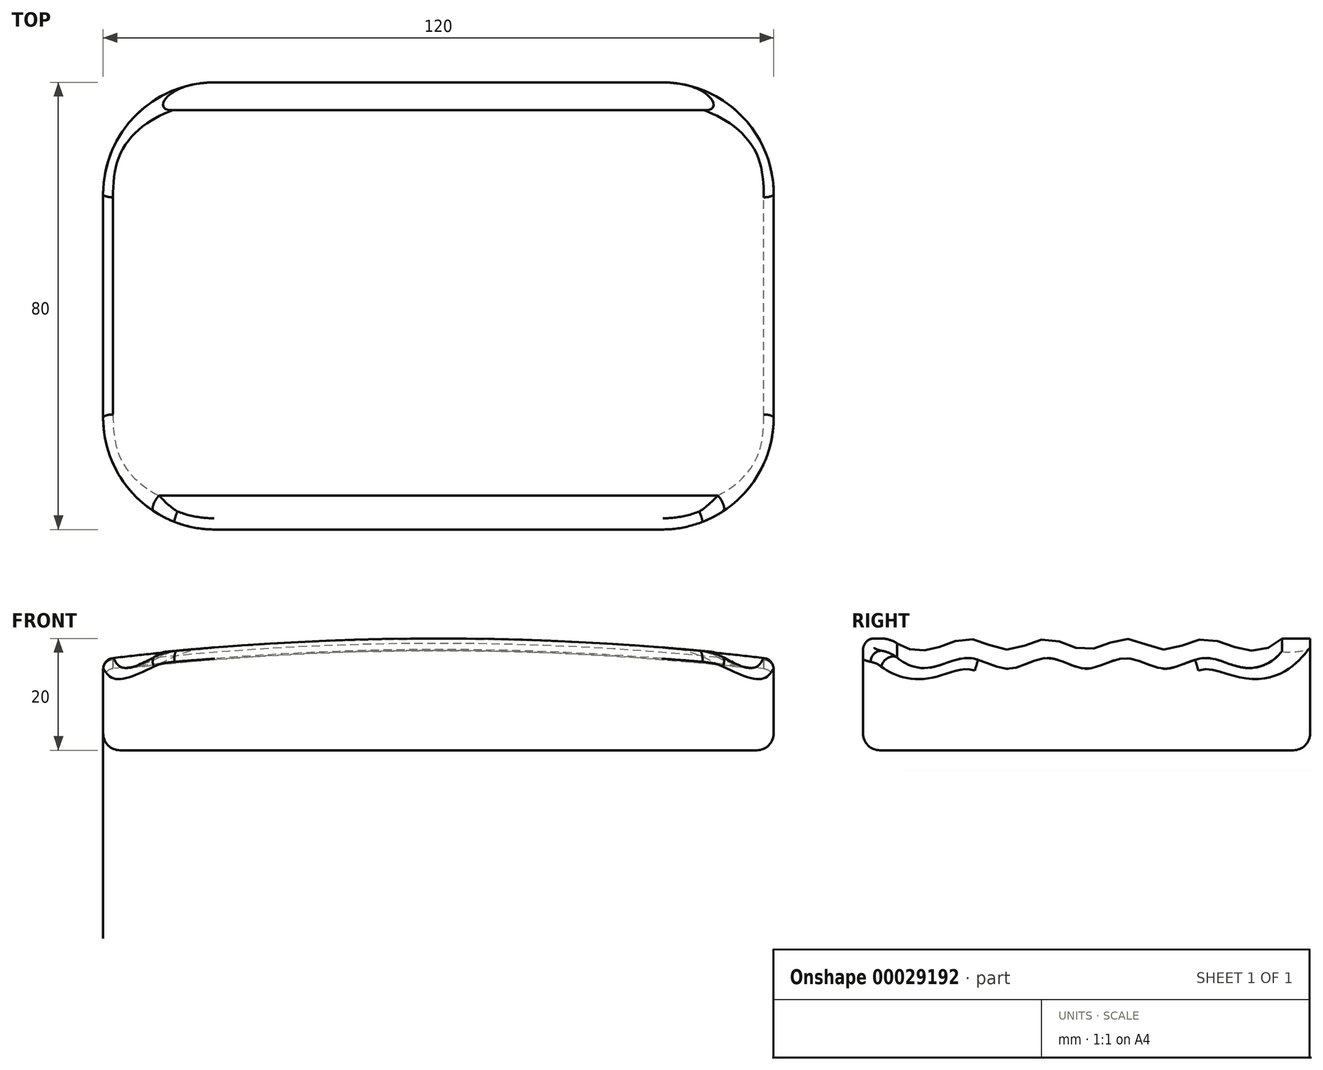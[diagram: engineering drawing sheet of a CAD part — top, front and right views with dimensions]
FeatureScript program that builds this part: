
annotation { "Feature Type Name" : "Feature", "Feature Type Description" : "" }
export const myFeature = defineFeature(function(context is Context, id is Id, definition is map)
    precondition{}
    {
        {
            var Q0;
            Q0=qCreatedBy(makeId("Top.planeOp"),FACE);
            var sketch = newSketch(context, id + "F0", { "sketchPlane" : qUnion([Q0])});
            skLineSegment(sketch, "E0.bottom", {"start": v(0, 0) * mm, "end": v(120, 0) * mm});
            skLineSegment(sketch, "E0.top", {"start": v(0, 80) * mm, "end": v(120, 80) * mm});
            skLineSegment(sketch, "E0.left", {"start": v(0, 0) * mm, "end": v(0, 80) * mm});
            skLineSegment(sketch, "E0.right", {"start": v(120, 0) * mm, "end": v(120, 80) * mm});
            skSolve(sketch);
        }
        {
            var Q0;
            Q0 = qSketchRegion(id + "F0", true);
            extrude(context, id + "F1", {"entities" : qUnion([Q0]), "depth" : 20 * mm});
        }
        {
            var Q0;
            Q0=makeQuery(id+"F1.opExtrude","SWEPT_FACE",FACE,{"disambiguationData":[OSD([sQuery(id+"F0.wireOp",EDGE,"E0.bottom")])]});
            var sketch = newSketch(context, id + "F2", { "sketchPlane" : qUnion([Q0])});
            skArc(sketch, "E1", {"start": v(120, 16.39) * mm, "mid": v(60, 20) * mm, "end": v(0, 16.39) * mm});
            skLineSegment(sketch, "E2", {"start": v(0, 16.39) * mm, "end": v(0, 47.47) * mm});
            skLineSegment(sketch, "E3", {"start": v(0, 47.47) * mm, "end": v(120, 47.47) * mm});
            skLineSegment(sketch, "E4", {"start": v(120, 47.47) * mm, "end": v(120, 16.39) * mm});
            skSolve(sketch);
        }
        {
            var Q0;
            Q0 = qSketchRegion(id + "F2", true);
            var Q1;
            Q1=makeQuery(id+"F1.opExtrude","SWEPT_FACE",FACE,{"disambiguationData":[OSD([sQuery(id+"F0.wireOp",EDGE,"E0.top")])]});
            extrude(context, id + "F3", {"entities" : qUnion([Q0]), "operationType" : NewBodyOperationType.REMOVE, "endBound" : BoundingType.UP_TO_SURFACE, "oppositeDirection" : true, "endBoundEntityFace" : qUnion([Q1]), "depth" : 25 * mm});
        }
        {
            var Q0;
            Q0=makeQuery(id+"F1.opExtrude","SWEPT_FACE",FACE,{"disambiguationData":[OSD([sQuery(id+"F0.wireOp",EDGE,"E0.left")])]});
            var sketch = newSketch(context, id + "F4", { "sketchPlane" : qUnion([Q0])});
            skLineSegment(sketch, "E5", {"start": v(-80, 16.39) * mm, "end": v(-80, 41.7) * mm});
            skLineSegment(sketch, "E6", {"start": v(-80, 41.7) * mm, "end": v(0, 41.7) * mm});
            skLineSegment(sketch, "E7", {"start": v(0, 41.7) * mm, "end": v(0, 16.39) * mm});
            skFitSpline(sketch, "E8", {"points": [v(-75, 16.39) * mm, v(-68, 14.39) * mm, v(-61, 16.29) * mm, v(-54, 14.39) * mm, v(-47, 16.29) * mm, v(-40, 14.39) * mm, v(-33, 16.29) * mm, v(-26, 14.39) * mm, v(-19, 16.29) * mm, v(-12, 14.39) * mm, v(-5, 16.39) * mm], "startDerivative": vector(59.91, -59.91) * mm, "endDerivative": vector(59.91, 59.91) * mm});
            skLineSegment(sketch, "E9", {"start": v(-75, 16.39) * mm, "end": v(-80, 16.39) * mm});
            skLineSegment(sketch, "E10", {"start": v(-5, 16.39) * mm, "end": v(0, 16.39) * mm});
            skSolve(sketch);
        }
        {
            var Q0;
            Q0=makeQuery(id+"F1.opExtrude","SWEPT_FACE",FACE,{"disambiguationData":[OSD([sQuery(id+"F0.wireOp",EDGE,"E0.bottom")])]});
            var sketch = newSketch(context, id + "F5", { "sketchPlane" : qUnion([Q0])});
            skCircle(sketch, "E11", {"center": v(60, -480) * mm, "radius": 500 * mm});
            skSolve(sketch);
        }
        {
            var Q0;
            {var subQ0=makeQuery(id+"F3.boolean.opBoolean","COPY",EDGE,{"derivedFrom":makeQuery(id+"F3.opExtrude","SWEPT_EDGE",EDGE,{"disambiguationData":[OSD([sQuery(id+"F0.wireOp",EDGE,"E0.bottom"),sQuery(id+"F0.wireOp",EDGE,"E0.left"),sQuery(id+"F2.wireOp",EDGE,"E1"),sQuery(id+"F2.wireOp",EDGE,"E2")])]})});var subQ1=sQuery(id+"F4.wireOp",EDGE,"E8");var subQ2=makeQuery(id+"F4.imprint","INTERSECT",VERTEX,{"disambiguationData":[OD(0.0)],"derivedFrom":[subQ0,subQ1]});Q0=makeQuery(id+"F4.imprint","IMPRINT",FACE,{"disambiguationData":[TD([[makeQuery(id+"F4.imprint","IMPRINT",EDGE,{"disambiguationData":[TD([[subQ2,1.0]])],"derivedFrom":subQ1}),1.0]])]});}
            var Q1;
            {var subQ0=makeQuery(id+"F3.boolean.opBoolean","COPY",EDGE,{"derivedFrom":makeQuery(id+"F3.opExtrude","SWEPT_EDGE",EDGE,{"disambiguationData":[OSD([sQuery(id+"F0.wireOp",EDGE,"E0.bottom"),sQuery(id+"F0.wireOp",EDGE,"E0.left"),sQuery(id+"F2.wireOp",EDGE,"E1"),sQuery(id+"F2.wireOp",EDGE,"E2")])]})});var subQ1=sQuery(id+"F4.wireOp",EDGE,"E8");var subQ3=makeQuery(id+"F4.imprint","INTERSECT",VERTEX,{"disambiguationData":[OD(1.0)],"derivedFrom":[subQ0,subQ1]});Q1=makeQuery(id+"F4.imprint","IMPRINT",FACE,{"disambiguationData":[TD([[makeQuery(id+"F4.imprint","IMPRINT",EDGE,{"disambiguationData":[TD([[subQ3,-1.0]])],"derivedFrom":subQ1}),1.0]])]});}
            var Q2;
            {var subQ0=makeQuery(id+"F3.boolean.opBoolean","COPY",EDGE,{"derivedFrom":makeQuery(id+"F3.opExtrude","SWEPT_EDGE",EDGE,{"disambiguationData":[OSD([sQuery(id+"F0.wireOp",EDGE,"E0.bottom"),sQuery(id+"F0.wireOp",EDGE,"E0.left"),sQuery(id+"F2.wireOp",EDGE,"E1"),sQuery(id+"F2.wireOp",EDGE,"E2")])]})});var subQ1=sQuery(id+"F4.wireOp",EDGE,"E8");var subQ3=makeQuery(id+"F4.imprint","INTERSECT",VERTEX,{"disambiguationData":[OD(3.0)],"derivedFrom":[subQ0,subQ1]});Q2=makeQuery(id+"F4.imprint","IMPRINT",FACE,{"disambiguationData":[TD([[makeQuery(id+"F4.imprint","IMPRINT",EDGE,{"disambiguationData":[TD([[subQ3,-1.0]])],"derivedFrom":subQ1}),1.0]])]});}
            var Q3;
            {var subQ0=makeQuery(id+"F3.boolean.opBoolean","COPY",EDGE,{"derivedFrom":makeQuery(id+"F3.opExtrude","SWEPT_EDGE",EDGE,{"disambiguationData":[OSD([sQuery(id+"F0.wireOp",EDGE,"E0.bottom"),sQuery(id+"F0.wireOp",EDGE,"E0.left"),sQuery(id+"F2.wireOp",EDGE,"E1"),sQuery(id+"F2.wireOp",EDGE,"E2")])]})});var subQ1=sQuery(id+"F4.wireOp",EDGE,"E8");var subQ3=makeQuery(id+"F4.imprint","INTERSECT",VERTEX,{"disambiguationData":[OD(5.0)],"derivedFrom":[subQ0,subQ1]});Q3=makeQuery(id+"F4.imprint","IMPRINT",FACE,{"disambiguationData":[TD([[makeQuery(id+"F4.imprint","IMPRINT",EDGE,{"disambiguationData":[TD([[subQ3,-1.0]])],"derivedFrom":subQ1}),1.0]])]});}
            var Q4;
            {var subQ0=makeQuery(id+"F3.boolean.opBoolean","COPY",EDGE,{"derivedFrom":makeQuery(id+"F3.opExtrude","SWEPT_EDGE",EDGE,{"disambiguationData":[OSD([sQuery(id+"F0.wireOp",EDGE,"E0.bottom"),sQuery(id+"F0.wireOp",EDGE,"E0.left"),sQuery(id+"F2.wireOp",EDGE,"E1"),sQuery(id+"F2.wireOp",EDGE,"E2")])]})});var subQ1=sQuery(id+"F4.wireOp",EDGE,"E8");var subQ2=makeQuery(id+"F4.imprint","INTERSECT",VERTEX,{"disambiguationData":[OD(7.0)],"derivedFrom":[subQ0,subQ1]});Q4=makeQuery(id+"F4.imprint","IMPRINT",FACE,{"disambiguationData":[TD([[makeQuery(id+"F4.imprint","IMPRINT",EDGE,{"disambiguationData":[TD([[subQ2,-1.0]])],"derivedFrom":subQ1}),1.0]])]});}
            var Q5;
            Q5=sQuery(id+"F5.wireOp",EDGE,"E11");
            sweep(context, id + "F6", {"operationType" : NewBodyOperationType.REMOVE, "profiles" : qUnion([Q0, Q1, Q2, Q3, Q4]), "path" : qUnion([Q5])});
        }
        {
            var Q0;
            Q0=makeQuery(id+"F1.opExtrude","SWEPT_EDGE",EDGE,{"disambiguationData":[OSD([sQuery(id+"F0.wireOp",EDGE,"E0.top"),sQuery(id+"F0.wireOp",EDGE,"E0.left")])]});
            var Q1;
            Q1=makeQuery(id+"F1.opExtrude","SWEPT_EDGE",EDGE,{"disambiguationData":[OSD([sQuery(id+"F0.wireOp",EDGE,"E0.bottom"),sQuery(id+"F0.wireOp",EDGE,"E0.left")])]});
            var Q2;
            Q2=makeQuery(id+"F1.opExtrude","SWEPT_EDGE",EDGE,{"disambiguationData":[OSD([sQuery(id+"F0.wireOp",EDGE,"E0.bottom"),sQuery(id+"F0.wireOp",EDGE,"E0.right")])]});
            var Q3;
            Q3=makeQuery(id+"F1.opExtrude","SWEPT_EDGE",EDGE,{"disambiguationData":[OSD([sQuery(id+"F0.wireOp",EDGE,"E0.top"),sQuery(id+"F0.wireOp",EDGE,"E0.right")])]});
            fillet(context, id + "F7", {"entities" : qUnion([Q0, Q1, Q2, Q3]), "radius" : 20 * mm, "tangentPropagation" : true, "allowEdgeOverflow" : false});
        }
        {
            var Q0;
            Q0=makeQuery(id+"F6.boolean.opBoolean","COPY",EDGE,{"derivedFrom":makeQuery(id+"F6.opSweep","SWEPT_EDGE",EDGE,{"disambiguationData":[OSD([sQuery(id+"F0.wireOp",EDGE,"E0.bottom"),sQuery(id+"F0.wireOp",EDGE,"E0.left"),sQuery(id+"F2.wireOp",EDGE,"E1"),sQuery(id+"F2.wireOp",EDGE,"E2"),sQuery(id+"F4.wireOp",EDGE,"E8"),sQuery(id+"F4.wireOp",EDGE,"E9"),sQuery(id+"F5.wireOp",EDGE,"E11")])]})});
            var Q1;
            Q1=makeQuery(id+"F6.boolean.opBoolean","COPY",EDGE,{"derivedFrom":makeQuery(id+"F6.opSweep","SWEPT_EDGE",EDGE,{"disambiguationData":[OSD([sQuery(id+"F0.wireOp",EDGE,"E0.bottom"),sQuery(id+"F0.wireOp",EDGE,"E0.left"),sQuery(id+"F2.wireOp",EDGE,"E1"),sQuery(id+"F2.wireOp",EDGE,"E2"),sQuery(id+"F4.wireOp",EDGE,"E8"),sQuery(id+"F4.wireOp",EDGE,"E10"),sQuery(id+"F5.wireOp",EDGE,"E11")])]})});
            fillet(context, id + "F8", {"entities" : qUnion([Q0, Q1]), "radius" : 5 * mm, "tangentPropagation" : true, "allowEdgeOverflow" : false});
        }
        {
            var Q0;
            Q0=makeQuery(id+"F7.opFillet","BLEND_EDGE",EDGE,{"blendedFrom":[makeQuery(id+"F1.opExtrude","SWEPT_EDGE",EDGE,{"disambiguationData":[OSD([sQuery(id+"F0.wireOp",EDGE,"E0.top"),sQuery(id+"F0.wireOp",EDGE,"E0.left")])]}),makeQuery(id+"F6.boolean.opBoolean","COPY",FACE,{"derivedFrom":makeQuery(id+"F6.opSweep","SWEPT_FACE",FACE,{"disambiguationData":[OSD([sQuery(id+"F4.wireOp",EDGE,"E8"),sQuery(id+"F5.wireOp",EDGE,"E11")])]})})],"blendedInto":[makeQuery(id+"F6.boolean.opBoolean","COPY",FACE,{"derivedFrom":makeQuery(id+"F6.opSweep","SWEPT_FACE",FACE,{"disambiguationData":[OSD([sQuery(id+"F4.wireOp",EDGE,"E8"),sQuery(id+"F5.wireOp",EDGE,"E11")])]})})]});
            fillet(context, id + "F9", {"entities" : qUnion([Q0]), "radius" : 2 * mm, "tangentPropagation" : true, "allowEdgeOverflow" : false});
        }
        {
            var Q0;
            Q0=makeQuery(id+"F1.opExtrude","CAP_EDGE",EDGE,{"disambiguationData":[OSD([sQuery(id+"F0.wireOp",EDGE,"E0.bottom")])],"isStart":true});
            fillet(context, id + "F10", {"entities" : qUnion([Q0]), "radius" : 3 * mm, "tangentPropagation" : true, "allowEdgeOverflow" : false});
        }
    });
